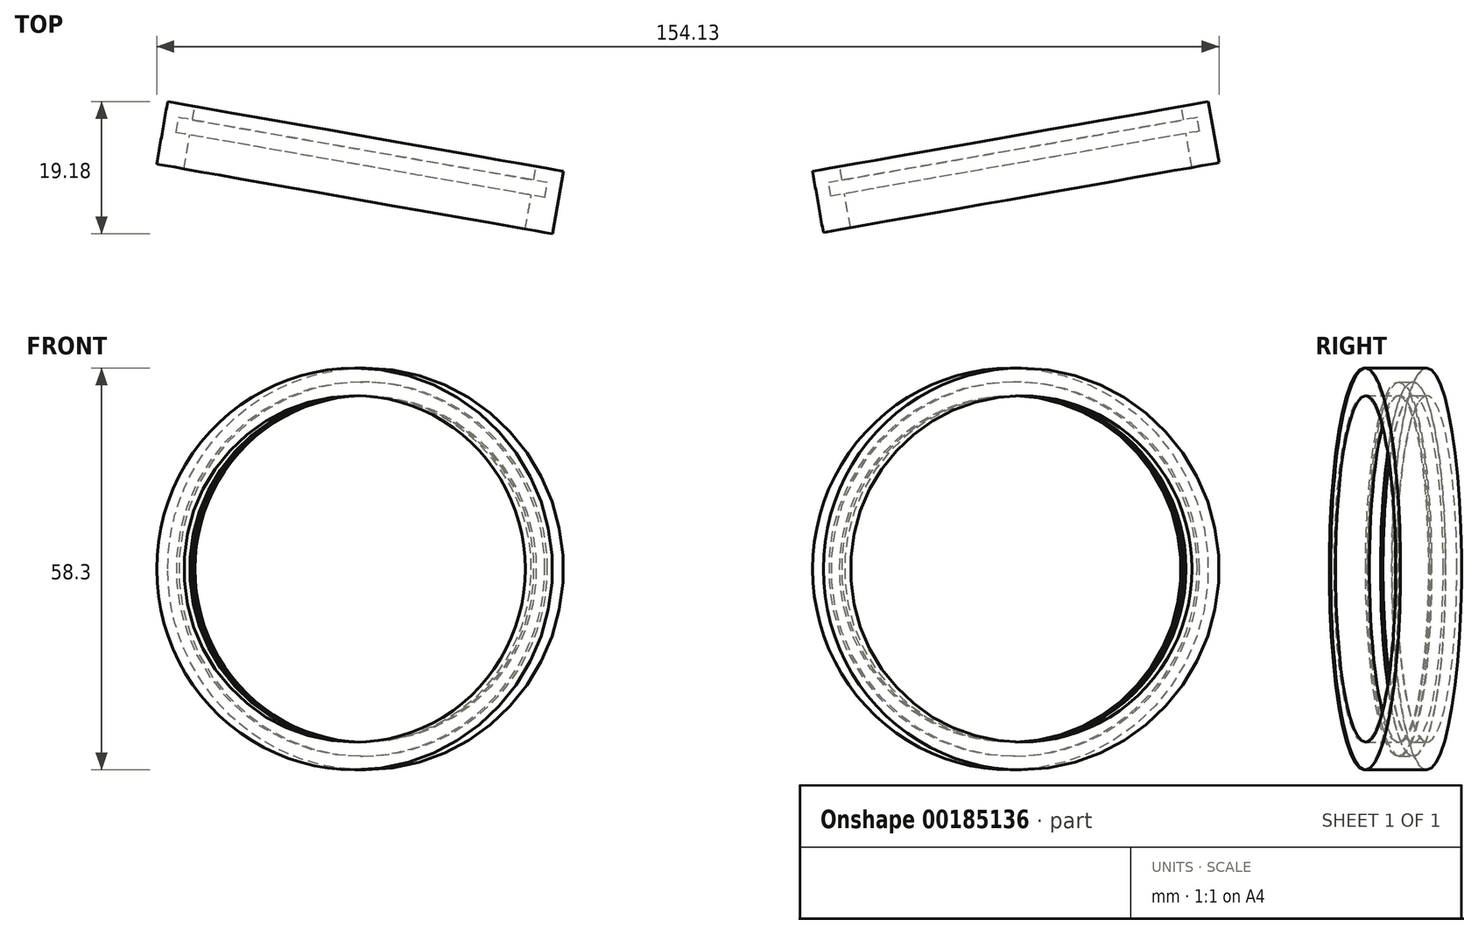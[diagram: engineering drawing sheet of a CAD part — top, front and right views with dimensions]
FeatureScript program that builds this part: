
annotation { "Feature Type Name" : "Feature", "Feature Type Description" : "" }
export const myFeature = defineFeature(function(context is Context, id is Id, definition is map)
    precondition{}
    {
        {
            var Q0;
            Q0=qCreatedBy(makeId("Front.planeOp"),FACE);
            var sketch = newSketch(context, id + "F0", { "sketchPlane" : qUnion([Q0])});
            skLineSegment(sketch, "E0", {"start": v(0, 36.22) * mm, "end": v(0, -35.6) * mm});
            skSolve(sketch);
        }
        {
            var Q0;
            Q0=sQuery(id+"F0.wireOp",EDGE,"E0");
            var Q1;
            Q1=qCreatedBy(makeId("Front.planeOp"),FACE);
            cPlane(context, id + "F1", {"entities" : qUnion([Q0, Q1]), "cplaneType" : CPlaneType.LINE_ANGLE, "offset" : 25.4 * mm, "angle" : 10 * degree, "width" : 152.4 * mm, "height" : 152.4 * mm});
        }
        {
            var Q0;
            Q0=qCreatedBy(id+"F1.planeOp",FACE);
            var sketch = newSketch(context, id + "F2", { "sketchPlane" : qUnion([Q0])});
            skCircle(sketch, "E1", {"center": v(47.5, 0) * mm, "radius": 25.15 * mm});
            skCircle(sketch, "E2", {"center": v(47.5, 0) * mm, "radius": 29.15 * mm});
            skSolve(sketch);
        }
        {
            var Q0;
            Q0=makeQuery(id+"F2.imprint","IMPRINT",FACE,{"disambiguationData":[TD([[makeQuery(id+"F2.imprint","IMPRINT",EDGE,{"derivedFrom":sQuery(id+"F2.wireOp",EDGE,"E1")}),-1.0]])]});
            extrude(context, id + "F3", {"entities" : qUnion([Q0]), "oppositeDirection" : true, "depth" : 2 * mm});
        }
        {
            var Q0;
            Q0=makeQuery(id+"F3.opExtrude","CAP_FACE",FACE,{"disambiguationData":[OSD([sQuery(id+"F2.wireOp",EDGE,"E1"),sQuery(id+"F2.wireOp",EDGE,"E2")])],"isStart":false});
            var sketch = newSketch(context, id + "F4", { "sketchPlane" : qUnion([Q0])});
            skCircle(sketch, "E3.0", {"center": v(-47.5, 0) * mm, "radius": 29.15 * mm});
            skCircle(sketch, "E4.0", {"center": v(-47.5, 0) * mm, "radius": 25.15 * mm});
            skCircle(sketch, "E5", {"center": v(-47.5, 0) * mm, "radius": 27.15 * mm});
            skSolve(sketch);
        }
        {
            var Q0;
            Q0=makeQuery(id+"F4.imprint","IMPRINT",FACE,{"disambiguationData":[TD([[makeQuery(id+"F4.imprint","IMPRINT",EDGE,{"derivedFrom":sQuery(id+"F4.wireOp",EDGE,"E3.0")}),-1.0]])]});
            extrude(context, id + "F5", {"entities" : qUnion([Q0]), "operationType" : NewBodyOperationType.ADD, "depth" : 2.2 * mm});
        }
        {
            var Q0;
            Q0=makeQuery(id+"F5.opExtrude","CAP_FACE",FACE,{"disambiguationData":[OSD([sQuery(id+"F4.wireOp",EDGE,"E3.0"),sQuery(id+"F4.wireOp",EDGE,"E5")])],"isStart":false});
            var sketch = newSketch(context, id + "F6", { "sketchPlane" : qUnion([Q0])});
            skCircle(sketch, "E6.0", {"center": v(-47.5, 0) * mm, "radius": 25.15 * mm});
            skCircle(sketch, "E7.0", {"center": v(-47.5, 0) * mm, "radius": 29.15 * mm});
            skSolve(sketch);
        }
        {
            var Q0;
            Q0=makeQuery(id+"F6.imprint","IMPRINT",FACE,{"disambiguationData":[TD([[makeQuery(id+"F6.imprint","IMPRINT",EDGE,{"derivedFrom":sQuery(id+"F6.wireOp",EDGE,"E6.0")}),-1.0]])]});
            var Q1;
            Q1=makeQuery(id+"F6.imprint","IMPRINT",FACE,{"disambiguationData":[TD([[makeQuery(id+"F6.imprint","IMPRINT",EDGE,{"derivedFrom":sQuery(id+"F6.wireOp",EDGE,"E7.0")}),-1.0]])]});
            extrude(context, id + "F7", {"entities" : qUnion([Q0, Q1]), "operationType" : NewBodyOperationType.ADD, "depth" : 5 * mm});
        }
        {
            var Q0;
            Q0=sQuery(id+"F0.wireOp",EDGE,"E0");
            var Q1;
            Q1=qCreatedBy(makeId("Front.planeOp"),FACE);
            cPlane(context, id + "F8", {"entities" : qUnion([Q0, Q1]), "cplaneType" : CPlaneType.LINE_ANGLE, "offset" : 25.4 * mm, "angle" : 350 * degree, "width" : 152.4 * mm, "height" : 152.4 * mm});
        }
        {
            var Q0;
            Q0=qCreatedBy(id+"F8.planeOp",FACE);
            var sketch = newSketch(context, id + "F9", { "sketchPlane" : qUnion([Q0])});
            skCircle(sketch, "E8", {"center": v(-47.5, 0) * mm, "radius": 29.15 * mm});
            skCircle(sketch, "E9", {"center": v(-47.5, 0) * mm, "radius": 25.15 * mm});
            skSolve(sketch);
        }
        {
            var Q0;
            Q0=makeQuery(id+"F9.imprint","IMPRINT",FACE,{"disambiguationData":[TD([[makeQuery(id+"F9.imprint","IMPRINT",EDGE,{"derivedFrom":sQuery(id+"F9.wireOp",EDGE,"E8")}),1.0]])]});
            extrude(context, id + "F10", {"entities" : qUnion([Q0]), "oppositeDirection" : true, "depth" : 2 * mm});
        }
        {
            var Q0;
            Q0=makeQuery(id+"F10.opExtrude","CAP_FACE",FACE,{"disambiguationData":[OSD([sQuery(id+"F9.wireOp",EDGE,"E8"),sQuery(id+"F9.wireOp",EDGE,"E9")])],"isStart":false});
            var sketch = newSketch(context, id + "F11", { "sketchPlane" : qUnion([Q0])});
            skCircle(sketch, "E10.0", {"center": v(47.5, 0) * mm, "radius": 25.15 * mm});
            skCircle(sketch, "E11.0", {"center": v(47.5, 0) * mm, "radius": 29.15 * mm});
            skCircle(sketch, "E12", {"center": v(47.5, 0) * mm, "radius": 27.15 * mm});
            skSolve(sketch);
        }
        {
            var Q0;
            Q0=makeQuery(id+"F11.imprint","IMPRINT",FACE,{"disambiguationData":[TD([[makeQuery(id+"F11.imprint","IMPRINT",EDGE,{"derivedFrom":sQuery(id+"F11.wireOp",EDGE,"E11.0")}),-1.0]])]});
            extrude(context, id + "F12", {"entities" : qUnion([Q0]), "operationType" : NewBodyOperationType.ADD, "depth" : 2 * mm});
        }
        {
            var Q0;
            Q0=makeQuery(id+"F12.opExtrude","CAP_FACE",FACE,{"disambiguationData":[OSD([sQuery(id+"F11.wireOp",EDGE,"E11.0"),sQuery(id+"F11.wireOp",EDGE,"E12")])],"isStart":false});
            var sketch = newSketch(context, id + "F13", { "sketchPlane" : qUnion([Q0])});
            skCircle(sketch, "E13.0", {"center": v(47.5, 0) * mm, "radius": 25.15 * mm});
            skCircle(sketch, "E14.0", {"center": v(47.5, 0) * mm, "radius": 29.15 * mm});
            skSolve(sketch);
        }
        {
            var Q0;
            Q0=makeQuery(id+"F13.imprint","IMPRINT",FACE,{"disambiguationData":[TD([[makeQuery(id+"F13.imprint","IMPRINT",EDGE,{"derivedFrom":sQuery(id+"F13.wireOp",EDGE,"E14.0")}),-1.0]])]});
            var Q1;
            Q1=makeQuery(id+"F13.imprint","IMPRINT",FACE,{"disambiguationData":[TD([[makeQuery(id+"F13.imprint","IMPRINT",EDGE,{"derivedFrom":sQuery(id+"F13.wireOp",EDGE,"E13.0")}),-1.0]])]});
            extrude(context, id + "F14", {"entities" : qUnion([Q0, Q1]), "operationType" : NewBodyOperationType.ADD, "depth" : 5 * mm});
        }
    });
